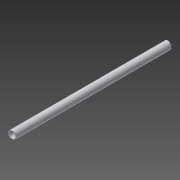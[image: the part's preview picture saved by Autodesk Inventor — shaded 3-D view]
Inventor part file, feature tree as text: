
AUTODESK INVENTOR PART (.ipt)
format: ipt  version: 2015 (Build 190159000, 159)  size: 106,496 bytes
history: native  units: mm
features: extrude x2, sketch x2, other x1, shell x1
ambient origin geometry x8: Origin, YZ Plane, XZ Plane, XY Plane, X Axis, Y Axis, Z Axis, Center Point
bodies: Body1 (feature_tree)
feature tree (6):
  other  "Bryła1"
  extrude  "Wyciągnięcie proste1"  Depth=20.0mm
  shell  "Skorupa1"  Thickness=400.0mm
  extrude  "Wyciągnięcie proste3"  Depth=2.0mm
  sketch  "Szkic1"
  sketch  "Szkic2"
